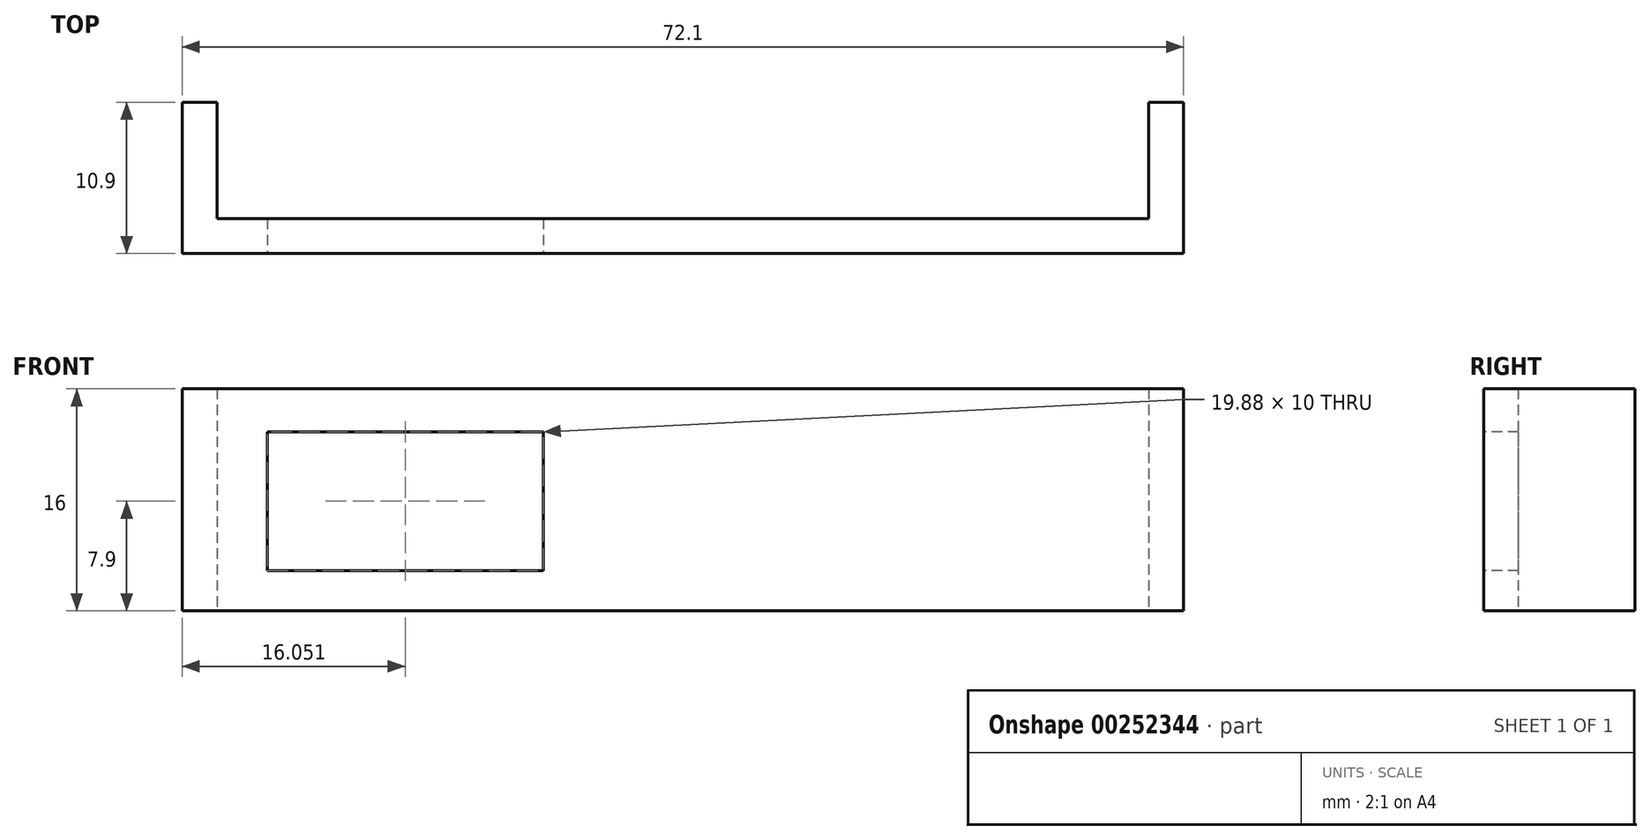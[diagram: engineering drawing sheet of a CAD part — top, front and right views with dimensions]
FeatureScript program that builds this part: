
annotation { "Feature Type Name" : "Feature", "Feature Type Description" : "" }
export const myFeature = defineFeature(function(context is Context, id is Id, definition is map)
    precondition{}
    {
        {
            var Q0;
            Q0=qCreatedBy(makeId("Front.planeOp"),FACE);
            var sketch = newSketch(context, id + "F0", { "sketchPlane" : qUnion([Q0])});
            skLineSegment(sketch, "E0.bottom", {"start": v(-36.56, 13.1) * mm, "end": v(35.54, 13.1) * mm});
            skLineSegment(sketch, "E0.top", {"start": v(-36.56, -2.9) * mm, "end": v(35.54, -2.9) * mm});
            skLineSegment(sketch, "E0.left", {"start": v(-36.56, 13.1) * mm, "end": v(-36.56, -2.9) * mm});
            skLineSegment(sketch, "E0.right", {"start": v(35.54, 13.1) * mm, "end": v(35.54, -2.9) * mm});
            skSolve(sketch);
        }
        {
            var Q0;
            Q0=makeQuery(id+"F0.imprint","IMPRINT",FACE,{"disambiguationData":[TD([[makeQuery(id+"F0.imprint","IMPRINT",EDGE,{"derivedFrom":sQuery(id+"F0.wireOp",EDGE,"E0.bottom")}),-1.0]])]});
            extrude(context, id + "F1", {"entities" : qUnion([Q0]), "depth" : 10.9 * mm});
        }
        {
            var Q0;
            Q0=makeQuery(id+"F1.opExtrude","CAP_FACE",FACE,{"disambiguationData":[OSD([sQuery(id+"F0.wireOp",EDGE,"E0.bottom"),sQuery(id+"F0.wireOp",EDGE,"E0.top"),sQuery(id+"F0.wireOp",EDGE,"E0.left"),sQuery(id+"F0.wireOp",EDGE,"E0.right")])],"isStart":true});
            var Q1;
            Q1=makeQuery(id+"F1.opExtrude","SWEPT_FACE",FACE,{"disambiguationData":[OSD([sQuery(id+"F0.wireOp",EDGE,"E0.bottom")])]});
            var Q2;
            Q2=makeQuery(id+"F1.opExtrude","SWEPT_FACE",FACE,{"disambiguationData":[OSD([sQuery(id+"F0.wireOp",EDGE,"E0.top")])]});
            shell(context, id + "F2", {"entities" : qUnion([Q0, Q1, Q2]), "thickness" : 2.5 * mm});
        }
        {
            var Q0;
            Q0=makeQuery(id+"F1.opExtrude","CAP_FACE",FACE,{"disambiguationData":[OSD([sQuery(id+"F0.wireOp",EDGE,"E0.bottom"),sQuery(id+"F0.wireOp",EDGE,"E0.top"),sQuery(id+"F0.wireOp",EDGE,"E0.left"),sQuery(id+"F0.wireOp",EDGE,"E0.right")])],"isStart":false});
            var sketch = newSketch(context, id + "F3", { "sketchPlane" : qUnion([Q0])});
            skLineSegment(sketch, "E1.bottom", {"start": v(-30.45, 10) * mm, "end": v(-10.57, 10) * mm});
            skLineSegment(sketch, "E1.top", {"start": v(-30.45, 0) * mm, "end": v(-10.57, 0) * mm});
            skLineSegment(sketch, "E1.left", {"start": v(-30.45, 10) * mm, "end": v(-30.45, 0) * mm});
            skLineSegment(sketch, "E1.right", {"start": v(-10.57, 10) * mm, "end": v(-10.57, 0) * mm});
            skSolve(sketch);
        }
        {
            var Q0;
            Q0=makeQuery(id+"F3.imprint","IMPRINT",FACE,{"disambiguationData":[TD([[makeQuery(id+"F3.imprint","IMPRINT",EDGE,{"derivedFrom":sQuery(id+"F3.wireOp",EDGE,"E1.bottom")}),-1.0]])]});
            extrude(context, id + "F4", {"entities" : qUnion([Q0]), "operationType" : NewBodyOperationType.REMOVE, "oppositeDirection" : true, "depth" : 25 * mm});
        }
    });
